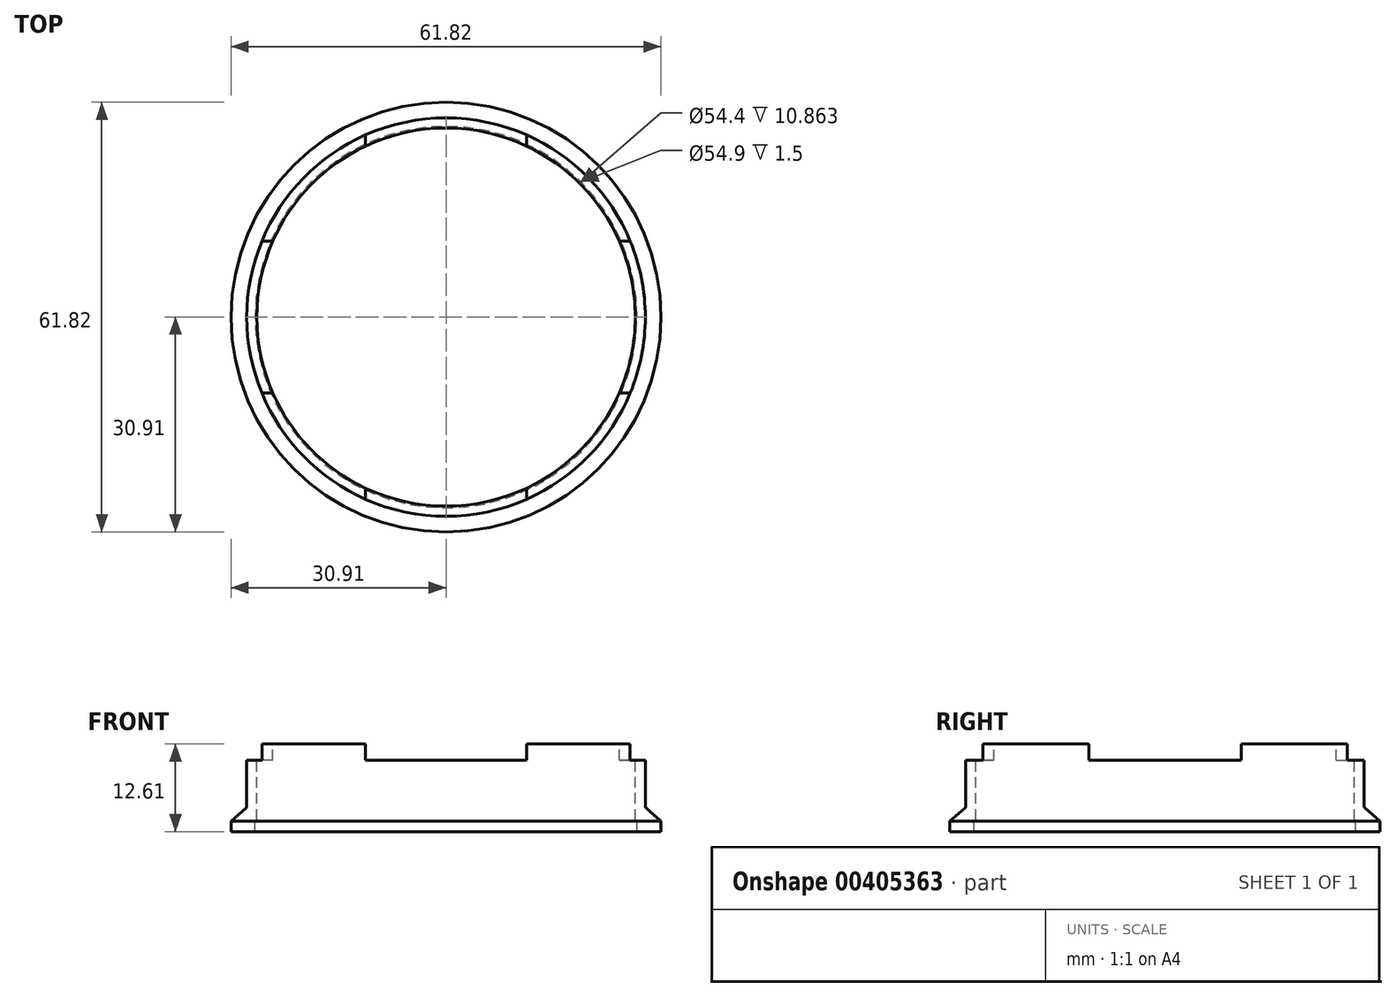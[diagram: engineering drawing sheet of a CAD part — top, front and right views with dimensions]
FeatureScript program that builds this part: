
annotation { "Feature Type Name" : "Feature", "Feature Type Description" : "" }
export const myFeature = defineFeature(function(context is Context, id is Id, definition is map)
    precondition{}
    {
        {
            var Q0;
            Q0=qCreatedBy(makeId("Front.planeOp"),FACE);
            var sketch = newSketch(context, id + "F0", { "sketchPlane" : qUnion([Q0])});
            skLineSegment(sketch, "E0", {"start": v(-30.91, 0) * mm, "end": v(-28.73, 1.93) * mm});
            skLineSegment(sketch, "E1", {"start": v(-28.65, 2.11) * mm, "end": v(-28.65, 11.11) * mm});
            skLineSegment(sketch, "E2", {"start": v(-27.2, 5) * mm, "end": v(-27.2, 10) * mm});
            skLineSegment(sketch, "E3", {"start": v(-27.2, 5) * mm, "end": v(-27.2, 0.25) * mm});
            skLineSegment(sketch, "E4", {"start": v(-27.45, 0) * mm, "end": v(-30.91, 0) * mm});
            skLineSegment(sketch, "E5", {"start": v(0, 35.52) * mm, "end": v(0, -14.65) * mm, "construction": true});
            skPoint(sketch, "E6.visualSharp", {"position": v(-28.65, 2) * mm});
            skArc(sketch, "E6.filletArc", {"start": v(-28.73, 1.93) * mm, "mid": v(-28.67, 2) * mm, "end": v(-28.65, 2.11) * mm});
            skPoint(sketch, "E7.visualSharp", {"position": v(-27.2, 0) * mm});
            skArc(sketch, "E7.filletArc", {"start": v(-27.45, 0) * mm, "mid": v(-27.27, 0.07) * mm, "end": v(-27.2, 0.25) * mm});
            skLineSegment(sketch, "E8", {"start": v(-28.65, 11.11) * mm, "end": v(-27.2, 11.11) * mm});
            skLineSegment(sketch, "E9", {"start": v(-27.2, 11.11) * mm, "end": v(-27.2, 10) * mm});
            skSolve(sketch);
        }
        {
            var Q0;
            Q0=makeQuery(id+"F0.imprint","IMPRINT",FACE,{"disambiguationData":[TD([[makeQuery(id+"F0.imprint","IMPRINT",EDGE,{"derivedFrom":sQuery(id+"F0.wireOp",EDGE,"E0")}),-1.0]])]});
            var Q1;
            Q1=sQuery(id+"F0.wireOp",EDGE,"E5");
            revolve(context, id + "F1", {"entities" : qUnion([Q0]), "axis" : qUnion([Q1]), "revolveType" : RevolveType.FULL});
        }
        {
            var Q0;
            Q0=qCreatedBy(makeId("Top.planeOp"),FACE);
            cPlane(context, id + "F2", {"entities" : qUnion([Q0]), "cplaneType" : CPlaneType.OFFSET, "offset" : 8.8 * mm, "width" : 150 * mm, "height" : 150 * mm});
        }
        {
            var Q0;
            Q0=qCreatedBy(id+"F2.planeOp",FACE);
            var sketch = newSketch(context, id + "F3", { "sketchPlane" : qUnion([Q0])});
            skLineSegment(sketch, "E10.bottom", {"start": v(11.58, -38.15) * mm, "end": v(-11.58, -38.15) * mm});
            skLineSegment(sketch, "E10.top", {"start": v(11.58, 38.15) * mm, "end": v(-11.58, 38.15) * mm});
            skLineSegment(sketch, "E10.left", {"start": v(11.58, -38.15) * mm, "end": v(11.58, 38.15) * mm});
            skLineSegment(sketch, "E10.right", {"start": v(-11.58, -38.15) * mm, "end": v(-11.58, 38.15) * mm});
            skPoint(sketch, "E10.middle", {"position": v(0, 0) * mm});
            skLineSegment(sketch, "E11.bottom", {"start": v(34.96, -10.95) * mm, "end": v(-34.96, -10.95) * mm});
            skLineSegment(sketch, "E11.top", {"start": v(34.96, 10.95) * mm, "end": v(-34.96, 10.95) * mm});
            skLineSegment(sketch, "E11.left", {"start": v(34.96, -10.95) * mm, "end": v(34.96, 10.95) * mm});
            skLineSegment(sketch, "E11.right", {"start": v(-34.96, -10.95) * mm, "end": v(-34.96, 10.95) * mm});
            skSolve(sketch);
        }
        {
            var Q0;
            {var subQ0=sQuery(id+"F3.wireOp",EDGE,"E10.top");Q0=makeQuery(id+"F3.imprint","IMPRINT",FACE,{"disambiguationData":[TD([[makeQuery(id+"F3.imprint","IMPRINT",EDGE,{"derivedFrom":subQ0}),1.0]])]});}
            var Q1;
            {var subQ5=sQuery(id+"F3.wireOp",EDGE,"E11.right");Q1=makeQuery(id+"F3.imprint","IMPRINT",FACE,{"disambiguationData":[TD([[makeQuery(id+"F3.imprint","IMPRINT",EDGE,{"derivedFrom":subQ5}),-1.0]])]});}
            var Q2;
            {var subQ5=sQuery(id+"F3.wireOp",EDGE,"E11.left");Q2=makeQuery(id+"F3.imprint","IMPRINT",FACE,{"disambiguationData":[TD([[makeQuery(id+"F3.imprint","IMPRINT",EDGE,{"derivedFrom":subQ5}),1.0]])]});}
            var Q3;
            {var subQ0=sQuery(id+"F3.wireOp",EDGE,"E10.bottom");Q3=makeQuery(id+"F3.imprint","IMPRINT",FACE,{"disambiguationData":[TD([[makeQuery(id+"F3.imprint","IMPRINT",EDGE,{"derivedFrom":subQ0}),-1.0]])]});}
            extrude(context, id + "F4", {"entities" : qUnion([Q0, Q1, Q2, Q3]), "operationType" : NewBodyOperationType.REMOVE, "depth" : 4 * mm});
        }
        {
            var Q0;
            Q0=makeQuery(id+"F1.opRevolve","SWEPT_FACE",FACE,{"disambiguationData":[OSD([sQuery(id+"F0.wireOp",EDGE,"E4")])]});
            extrude(context, id + "F5", {"entities" : qUnion([Q0]), "operationType" : NewBodyOperationType.ADD, "depth" : 1.5 * mm});
        }
    });
